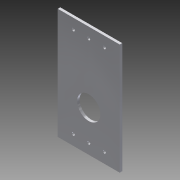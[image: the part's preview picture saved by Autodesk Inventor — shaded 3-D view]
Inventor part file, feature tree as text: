
AUTODESK INVENTOR PART (.ipt)
format: ipt  version: 2015 (Build 190159000, 159)  size: 134,656 bytes
history: native  units: in
note: dims shown in document units (in); Inventor stores cm internally (conversion verified against a paired STEP export)
features: other x4, hole x2
ambient origin geometry x8: Origin, YZ Plane, XZ Plane, XY Plane, X Axis, Y Axis, Z Axis, Center Point
bodies: Solid1 (feature_tree)
feature tree (6):
  hole  "rivet_holes"  [1 undecoded]
  hole  "bearing_hole"  [1 undecoded]
  other  "face_sketch"
  other  "Plate1"
  other  "rivet_holes_sketch"
  other  "bearing_hole_sketch"
note: 2 required parameter values undecoded (feature->parameter linkage not recoverable at this tier; creation-order binding heuristic only, values carry confidence <= 0.55)
